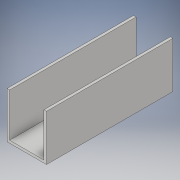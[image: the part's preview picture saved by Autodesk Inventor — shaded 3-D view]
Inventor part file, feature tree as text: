
AUTODESK INVENTOR PART (.ipt)
format: ipt  version: 2017 (Build 210142000, 142)  size: 94,720 bytes
history: native  units: in
note: dims shown in document units (in); Inventor stores cm internally (conversion verified against a paired STEP export)
features: extrude x1, sketch x1
ambient origin geometry x8: Origin, YZ Plane, XZ Plane, XY Plane, X Axis, Y Axis, Z Axis, Center Point
bodies: Solid1 (feature_tree)
feature tree (2):
  extrude  "Extrusion1"  Depth=12.0in TaperAngle=0.0deg
  sketch  "Sketch1"  dims[d2=0.25in d5=12.0in d6=0.0in d7=4.3755in d8=3.75in d9=0.25in d10=4.126in]
